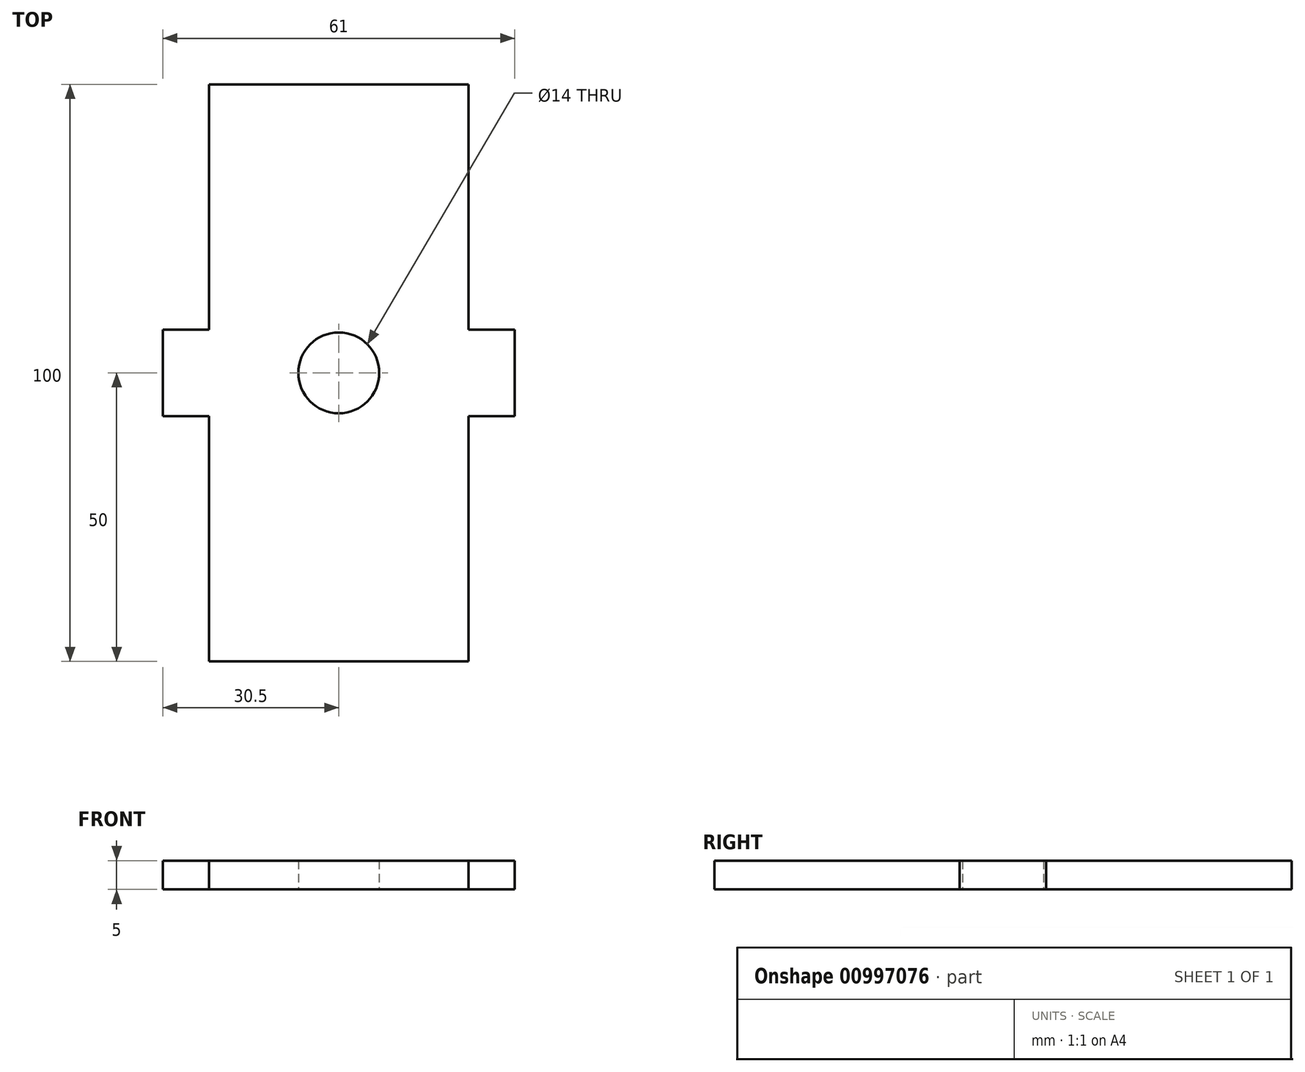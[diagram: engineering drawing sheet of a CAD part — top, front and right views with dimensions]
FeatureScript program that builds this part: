
annotation { "Feature Type Name" : "Feature", "Feature Type Description" : "" }
export const myFeature = defineFeature(function(context is Context, id is Id, definition is map)
    precondition{}
    {
        {
            var Q0;
            Q0=qCreatedBy(makeId("Top.planeOp"),FACE);
            var sketch = newSketch(context, id + "F0", { "sketchPlane" : qUnion([Q0])});
            skLineSegment(sketch, "E0", {"start": v(-30.5, 7.5) * mm, "end": v(-30.5, -7.5) * mm});
            skLineSegment(sketch, "E1", {"start": v(-30.5, -7.5) * mm, "end": v(-22.5, -7.5) * mm});
            skLineSegment(sketch, "E2", {"start": v(-22.5, -7.5) * mm, "end": v(-22.5, -50) * mm});
            skLineSegment(sketch, "E3", {"start": v(-22.5, -50) * mm, "end": v(0, -50) * mm});
            skLineSegment(sketch, "E4", {"start": v(0, -50) * mm, "end": v(0, -7) * mm});
            skLineSegment(sketch, "E5", {"start": v(0, 50) * mm, "end": v(-22.5, 50) * mm});
            skLineSegment(sketch, "E6", {"start": v(-22.5, 50) * mm, "end": v(-22.5, 7.5) * mm});
            skLineSegment(sketch, "E7", {"start": v(-22.5, 7.5) * mm, "end": v(-30.5, 7.5) * mm});
            skPoint(sketch, "E8", {"position": v(-30.5, 0) * mm});
            skPoint(sketch, "E9", {"position": v(0, 0) * mm});
            skLineSegment(sketch, "E10.MirrorCS", {"start": v(22.5, 7.5) * mm, "end": v(30.5, 7.5) * mm});
            skLineSegment(sketch, "E11.MirrorCS", {"start": v(30.5, -7.5) * mm, "end": v(22.5, -7.5) * mm});
            skLineSegment(sketch, "E12.MirrorCS", {"start": v(30.5, 7.5) * mm, "end": v(30.5, -7.5) * mm});
            skLineSegment(sketch, "E13.MirrorCS", {"start": v(22.5, -7.5) * mm, "end": v(22.5, -50) * mm});
            skPoint(sketch, "E14.MirrorP", {"position": v(30.5, 0) * mm});
            skLineSegment(sketch, "E15.MirrorCS", {"start": v(22.5, -50) * mm, "end": v(0, -50) * mm});
            skLineSegment(sketch, "E16.MirrorCS", {"start": v(0, 50) * mm, "end": v(22.5, 50) * mm});
            skLineSegment(sketch, "E17.MirrorCS", {"start": v(22.5, 50) * mm, "end": v(22.5, 7.5) * mm});
            skLineSegment(sketch, "E18.MirrorCS", {"start": v(0, -50) * mm, "end": v(0, 50) * mm});
            skCircle(sketch, "E19", {"center": v(0, 0) * mm, "radius": 7 * mm});
            skLineSegment(sketch, "E20.trimOffspring", {"start": v(0, 7) * mm, "end": v(0, 50) * mm});
            skSolve(sketch);
        }
        {
            var Q0;
            Q0 = qSketchRegion(id + "F0", true);
            extrude(context, id + "F1", {"entities" : qUnion([Q0]), "depth" : 5 * mm, "offsetDistance" : 25 * mm});
        }
    });
